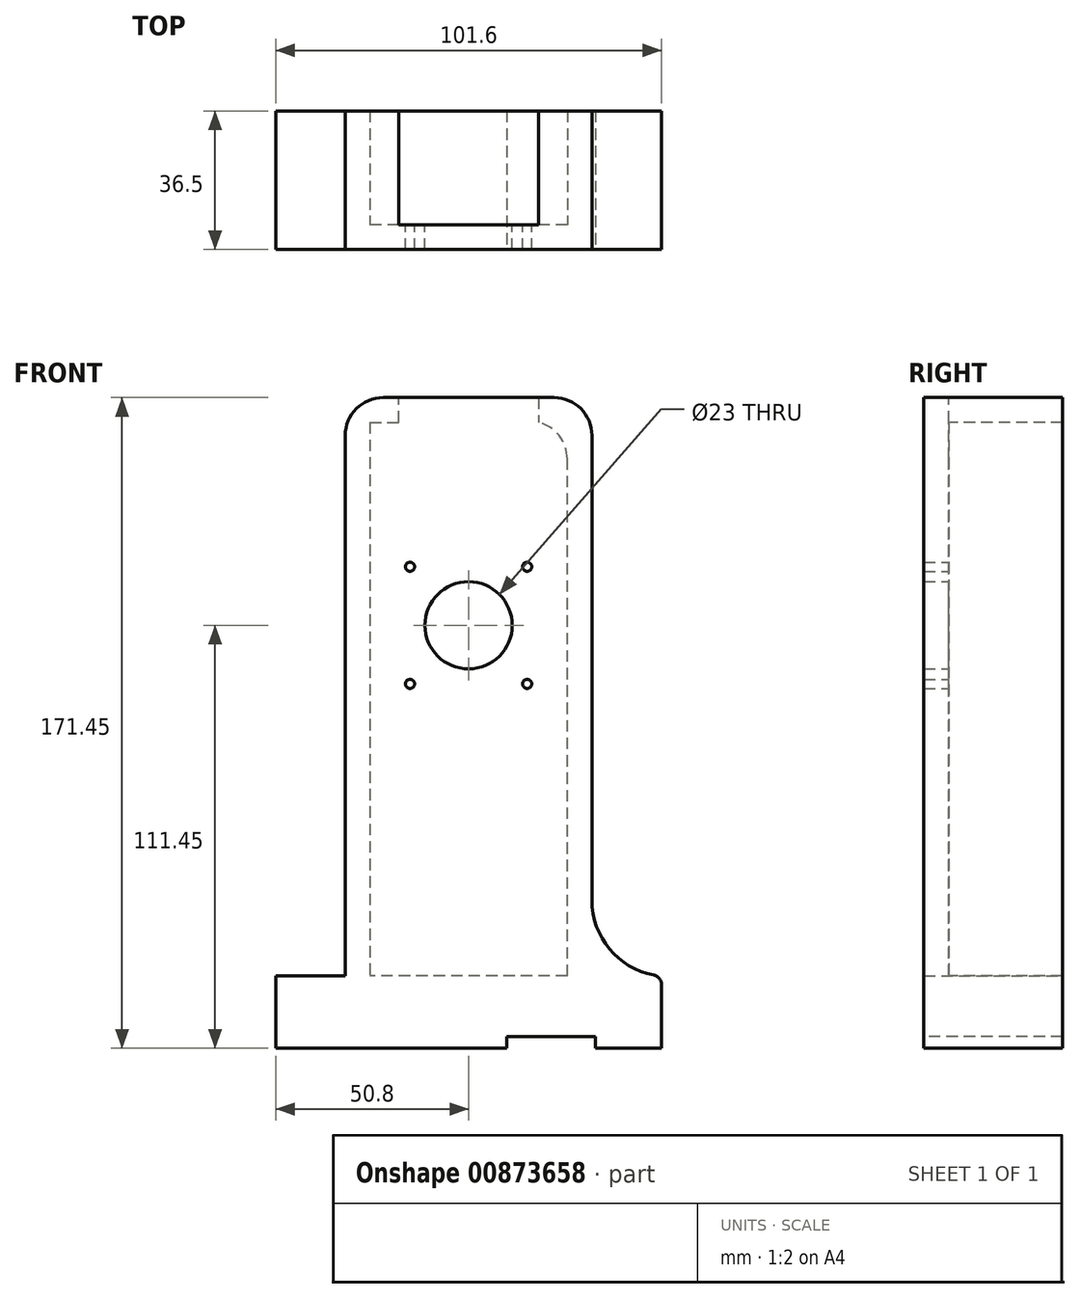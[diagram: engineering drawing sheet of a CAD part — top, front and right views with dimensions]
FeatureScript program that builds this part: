
annotation { "Feature Type Name" : "Feature", "Feature Type Description" : "" }
export const myFeature = defineFeature(function(context is Context, id is Id, definition is map)
    precondition{}
    {
        {
            var Q0;
            Q0=qCreatedBy(makeId("Front.planeOp"),FACE);
            var sketch = newSketch(context, id + "F0", { "sketchPlane" : qUnion([Q0])});
            skLineSegment(sketch, "E0.bottom", {"start": v(-32.5, 76.2) * mm, "end": v(32.5, 76.2) * mm});
            skLineSegment(sketch, "E0.top", {"start": v(-32.5, -76.2) * mm, "end": v(32.5, -76.2) * mm});
            skLineSegment(sketch, "E0.left", {"start": v(-32.5, 76.2) * mm, "end": v(-32.5, -76.2) * mm});
            skLineSegment(sketch, "E0.right", {"start": v(32.5, 76.2) * mm, "end": v(32.5, -76.2) * mm});
            skPoint(sketch, "E0.middle", {"position": v(0, 0) * mm});
            skLineSegment(sketch, "E1", {"start": v(0, 76.2) * mm, "end": v(0, -76.2) * mm, "construction": true});
            skLineSegment(sketch, "E2.bottom", {"start": v(-15.43, 31.63) * mm, "end": v(15.43, 31.63) * mm, "construction": true});
            skLineSegment(sketch, "E2.top", {"start": v(-15.43, 0.77) * mm, "end": v(15.43, 0.77) * mm, "construction": true});
            skLineSegment(sketch, "E2.left", {"start": v(-15.43, 31.63) * mm, "end": v(-15.43, 0.77) * mm, "construction": true});
            skLineSegment(sketch, "E2.right", {"start": v(15.43, 31.63) * mm, "end": v(15.43, 0.77) * mm, "construction": true});
            skPoint(sketch, "E2.middle", {"position": v(0, 16.2) * mm});
            skCircle(sketch, "E3", {"center": v(-15.43, 31.63) * mm, "radius": 1.2 * mm});
            skCircle(sketch, "E4", {"center": v(15.43, 31.63) * mm, "radius": 1.2 * mm});
            skCircle(sketch, "E5", {"center": v(15.43, 0.77) * mm, "radius": 1.2 * mm});
            skCircle(sketch, "E6", {"center": v(-15.43, 0.77) * mm, "radius": 1.2 * mm});
            skCircle(sketch, "E7", {"center": v(0, 16.2) * mm, "radius": 11.5 * mm});
            skSolve(sketch);
        }
        {
            var Q0;
            Q0=makeQuery(id+"F0.imprint","IMPRINT",FACE,{"disambiguationData":[TD([[makeQuery(id+"F0.imprint","IMPRINT",EDGE,{"derivedFrom":sQuery(id+"F0.wireOp",EDGE,"E0.bottom")}),-1.0]])]});
            extrude(context, id + "F1", {"entities" : qUnion([Q0]), "depth" : 6.5 * mm, "offsetDistance" : 25.4 * mm});
        }
        {
            var Q0;
            Q0=makeQuery(id+"F1.opExtrude","CAP_FACE",FACE,{"disambiguationData":[OSD([sQuery(id+"F0.wireOp",EDGE,"E0.bottom"),sQuery(id+"F0.wireOp",EDGE,"E0.top"),sQuery(id+"F0.wireOp",EDGE,"E0.left"),sQuery(id+"F0.wireOp",EDGE,"E0.right"),sQuery(id+"F0.wireOp",EDGE,"E3"),sQuery(id+"F0.wireOp",EDGE,"E4"),sQuery(id+"F0.wireOp",EDGE,"E5"),sQuery(id+"F0.wireOp",EDGE,"E6"),sQuery(id+"F0.wireOp",EDGE,"E7")])],"isStart":true});
            var sketch = newSketch(context, id + "F2", { "sketchPlane" : qUnion([Q0])});
            skLineSegment(sketch, "E8", {"start": v(-32.5, 76.2) * mm, "end": v(-32.5, -76.2) * mm});
            skLineSegment(sketch, "E9", {"start": v(-32.5, -76.2) * mm, "end": v(-26, -76.2) * mm});
            skLineSegment(sketch, "E10", {"start": v(-26, -76.2) * mm, "end": v(-26, 69.7) * mm});
            skLineSegment(sketch, "E11", {"start": v(26, 69.7) * mm, "end": v(26, -76.2) * mm});
            skLineSegment(sketch, "E12", {"start": v(26, -76.2) * mm, "end": v(32.5, -76.2) * mm});
            skLineSegment(sketch, "E13", {"start": v(32.5, -76.2) * mm, "end": v(32.5, 76.2) * mm});
            skLineSegment(sketch, "E14", {"start": v(-32.5, 76.2) * mm, "end": v(-18.41, 76.2) * mm});
            skLineSegment(sketch, "E15", {"start": v(26, 69.7) * mm, "end": v(18.38, 69.7) * mm});
            skLineSegment(sketch, "E16", {"start": v(18.38, 69.7) * mm, "end": v(18.38, 76.2) * mm});
            skLineSegment(sketch, "E17", {"start": v(18.38, 76.2) * mm, "end": v(32.5, 76.2) * mm});
            skLineSegment(sketch, "E18", {"start": v(-18.41, 76.2) * mm, "end": v(-18.41, 69.7) * mm});
            skLineSegment(sketch, "E19", {"start": v(-26, 69.7) * mm, "end": v(-18.41, 69.7) * mm});
            skSolve(sketch);
        }
        {
            var Q0;
            Q0=makeQuery(id+"F2.imprint","IMPRINT",FACE,{"disambiguationData":[TD([[makeQuery(id+"F2.imprint","IMPRINT",EDGE,{"derivedFrom":sQuery(id+"F2.wireOp",EDGE,"E8")}),1.0]])]});
            extrude(context, id + "F3", {"entities" : qUnion([Q0]), "operationType" : NewBodyOperationType.ADD, "depth" : 30 * mm, "offsetDistance" : 25.4 * mm});
        }
        {
            var Q0;
            Q0=makeQuery(id+"F3.boolean.opBoolean","MERGE",EDGE,{"derivedFrom":[makeQuery(id+"F1.opExtrude","SWEPT_EDGE",EDGE,{"disambiguationData":[OSD([sQuery(id+"F0.wireOp",EDGE,"E0.bottom"),sQuery(id+"F0.wireOp",EDGE,"E0.right")])]}),makeQuery(id+"F3.opExtrude","SWEPT_EDGE",EDGE,{"disambiguationData":[OSD([sQuery(id+"F2.wireOp",EDGE,"E8"),sQuery(id+"F2.wireOp",EDGE,"top9ZBjK-HaFo-sFNs-O2iO-FRZwXBmGVt9y")])]})]});
            var Q1;
            Q1=makeQuery(id+"F3.boolean.opBoolean","MERGE",EDGE,{"derivedFrom":[makeQuery(id+"F1.opExtrude","SWEPT_EDGE",EDGE,{"disambiguationData":[OSD([sQuery(id+"F0.wireOp",EDGE,"E0.bottom"),sQuery(id+"F0.wireOp",EDGE,"E0.left")])]}),makeQuery(id+"F3.opExtrude","SWEPT_EDGE",EDGE,{"disambiguationData":[OSD([sQuery(id+"F2.wireOp",EDGE,"E13"),sQuery(id+"F2.wireOp",EDGE,"top9ZBjK-HaFo-sFNs-O2iO-FRZwXBmGVt9y")])]})]});
            var Q2;
            Q2=makeQuery(id+"F3.opExtrude","SWEPT_EDGE",EDGE,{"disambiguationData":[OSD([sQuery(id+"F2.wireOp",EDGE,"E10"),sQuery(id+"F2.wireOp",EDGE,"qCY2hAou-IPp3-AkAy-DybL-IcWh8WlS5N6P")])]});
            var Q3;
            Q3=makeQuery(id+"F3.opExtrude","SWEPT_EDGE",EDGE,{"disambiguationData":[OSD([sQuery(id+"F2.wireOp",EDGE,"qCY2hAou-IPp3-AkAy-DybL-IcWh8WlS5N6P"),sQuery(id+"F2.wireOp",EDGE,"E11")])]});
            fillet(context, id + "F4", {"entities" : qUnion([Q0, Q1, Q2, Q3]), "radius" : 10 * mm, "tangentPropagation" : true, "allowEdgeOverflow" : false});
        }
        {
            var Q0;
            Q0=qCreatedBy(makeId("Front.planeOp"),FACE);
            var sketch = newSketch(context, id + "F5", { "sketchPlane" : qUnion([Q0])});
            skLineSegment(sketch, "E20", {"start": v(0, 0) * mm, "end": v(0, -76.2) * mm, "construction": true});
            skLineSegment(sketch, "E21", {"start": v(0, -76.2) * mm, "end": v(0, -95.25) * mm, "construction": true});
            skLineSegment(sketch, "E22.bottom", {"start": v(-50.8, -95.25) * mm, "end": v(50.8, -95.25) * mm});
            skLineSegment(sketch, "E22.top", {"start": v(-50.8, -76.2) * mm, "end": v(50.8, -76.2) * mm});
            skLineSegment(sketch, "E22.left", {"start": v(-50.8, -95.25) * mm, "end": v(-50.8, -76.2) * mm});
            skLineSegment(sketch, "E22.right", {"start": v(50.8, -95.25) * mm, "end": v(50.8, -76.2) * mm});
            skPoint(sketch, "E22.middle", {"position": v(0, -85.72) * mm});
            skSolve(sketch);
        }
        {
            var Q0;
            Q0=makeQuery(id+"F5.imprint","IMPRINT",FACE,{"disambiguationData":[TD([[makeQuery(id+"F5.imprint","IMPRINT",EDGE,{"derivedFrom":sQuery(id+"F5.wireOp",EDGE,"E22.bottom")}),1.0]])]});
            extrude(context, id + "F6", {"entities" : qUnion([Q0]), "operationType" : NewBodyOperationType.ADD, "depth" : 6.5 * mm, "offsetDistance" : 25.4 * mm});
        }
        {
            var Q0;
            Q0=makeQuery(id+"F6.boolean.opBoolean","MERGE",FACE,{"derivedFrom":[makeQuery(id+"F1.opExtrude","CAP_FACE",FACE,{"disambiguationData":[OSD([sQuery(id+"F0.wireOp",EDGE,"E0.bottom"),sQuery(id+"F0.wireOp",EDGE,"E0.top"),sQuery(id+"F0.wireOp",EDGE,"E0.left"),sQuery(id+"F0.wireOp",EDGE,"E0.right"),sQuery(id+"F0.wireOp",EDGE,"E3"),sQuery(id+"F0.wireOp",EDGE,"E4"),sQuery(id+"F0.wireOp",EDGE,"E5"),sQuery(id+"F0.wireOp",EDGE,"E6"),sQuery(id+"F0.wireOp",EDGE,"E7")])],"isStart":true}),makeQuery(id+"F6.opExtrude","CAP_FACE",FACE,{"disambiguationData":[OSD([sQuery(id+"F5.wireOp",EDGE,"E22.bottom"),sQuery(id+"F5.wireOp",EDGE,"E22.top"),sQuery(id+"F5.wireOp",EDGE,"E22.left"),sQuery(id+"F5.wireOp",EDGE,"E22.right")])],"isStart":true})]});
            var sketch = newSketch(context, id + "F7", { "sketchPlane" : qUnion([Q0])});
            skLineSegment(sketch, "E23.bottom", {"start": v(-50.8, -76.2) * mm, "end": v(50.8, -76.2) * mm});
            skLineSegment(sketch, "E23.top", {"start": v(-50.8, -95.25) * mm, "end": v(50.8, -95.25) * mm});
            skLineSegment(sketch, "E23.left", {"start": v(-50.8, -76.2) * mm, "end": v(-50.8, -95.25) * mm});
            skLineSegment(sketch, "E23.right", {"start": v(50.8, -76.2) * mm, "end": v(50.8, -95.25) * mm});
            skPoint(sketch, "E23.middle", {"position": v(0, -85.72) * mm});
            skPoint(sketch, "E23.middle.positionSnap0", {"position": v(-50.8, -85.72) * mm});
            skPoint(sketch, "E23.centerSnap0", {"position": v(-50.8, -85.72) * mm});
            skSolve(sketch);
        }
        {
            var Q0;
            Q0 = qSketchRegion(id + "F7", true);
            extrude(context, id + "F8", {"entities" : qUnion([Q0]), "operationType" : NewBodyOperationType.ADD, "depth" : 30 * mm, "offsetDistance" : 25.4 * mm});
        }
        {
            var Q0;
            {var subQ0=sQuery(id+"F0.wireOp",EDGE,"E0.left");var subQ2=sQuery(id+"F2.wireOp",EDGE,"E13");var subQ4=sQuery(id+"F2.wireOp",EDGE,"E12");var subQ5=sQuery(id+"F0.wireOp",EDGE,"E0.top");var subQ6=makeQuery(id+"F3.boolean.opBoolean","MERGE",EDGE,{"derivedFrom":[makeQuery(id+"F1.opExtrude","SWEPT_EDGE",EDGE,{"disambiguationData":[OSD([subQ5,subQ0])]}),makeQuery(id+"F3.opExtrude","SWEPT_EDGE",EDGE,{"disambiguationData":[OSD([subQ4,subQ2])]})]});Q0=makeQuery(id+"F8.boolean.opBoolean","MERGE",EDGE,{"derivedFrom":[makeQuery(id+"F6.boolean.opBoolean","SPLIT",EDGE,{"disambiguationData":[topologyDisambiguationEdgeConnected([makeQuery(id+"F1.opExtrude","SWEPT_FACE",FACE,{"disambiguationData":[OSD([subQ5])]})])],"derivedFrom":subQ6}),makeQuery(id+"F6.boolean.opBoolean","SPLIT",EDGE,{"disambiguationData":[topologyDisambiguationEdgeConnected([makeQuery(id+"F6.opExtrude","SWEPT_FACE",FACE,{"disambiguationData":[OSD([sQuery(id+"F5.wireOp",EDGE,"E22.top")])]})])],"derivedFrom":subQ6})]});}
            var Q1;
            {var subQ0=sQuery(id+"F0.wireOp",EDGE,"E0.right");var subQ2=sQuery(id+"F2.wireOp",EDGE,"E8");var subQ4=sQuery(id+"F2.wireOp",EDGE,"E9");var subQ5=sQuery(id+"F0.wireOp",EDGE,"E0.top");var subQ6=makeQuery(id+"F3.boolean.opBoolean","MERGE",EDGE,{"derivedFrom":[makeQuery(id+"F1.opExtrude","SWEPT_EDGE",EDGE,{"disambiguationData":[OSD([subQ5,subQ0])]}),makeQuery(id+"F3.opExtrude","SWEPT_EDGE",EDGE,{"disambiguationData":[OSD([subQ2,subQ4])]})]});Q1=makeQuery(id+"F8.boolean.opBoolean","MERGE",EDGE,{"derivedFrom":[makeQuery(id+"F6.boolean.opBoolean","SPLIT",EDGE,{"disambiguationData":[topologyDisambiguationEdgeConnected([makeQuery(id+"F1.opExtrude","SWEPT_FACE",FACE,{"disambiguationData":[OSD([subQ5])]})])],"derivedFrom":subQ6}),makeQuery(id+"F6.boolean.opBoolean","SPLIT",EDGE,{"disambiguationData":[topologyDisambiguationEdgeConnected([makeQuery(id+"F6.opExtrude","SWEPT_FACE",FACE,{"disambiguationData":[OSD([sQuery(id+"F5.wireOp",EDGE,"E22.top")])]})])],"derivedFrom":subQ6})]});}
            fillet(context, id + "F9", {"entities" : qUnion([Q0, Q1]), "radius" : 20 * mm, "tangentPropagation" : true, "allowEdgeOverflow" : false});
        }
        {
            var Q0;
            {var subQ0=sQuery(id+"F0.wireOp",EDGE,"E0.left");var subQ2=sQuery(id+"F2.wireOp",EDGE,"E13");var subQ4=sQuery(id+"F2.wireOp",EDGE,"E12");var subQ5=sQuery(id+"F0.wireOp",EDGE,"E0.top");var subQ6=makeQuery(id+"F3.boolean.opBoolean","MERGE",EDGE,{"derivedFrom":[makeQuery(id+"F1.opExtrude","SWEPT_EDGE",EDGE,{"disambiguationData":[OSD([subQ5,subQ0])]}),makeQuery(id+"F3.opExtrude","SWEPT_EDGE",EDGE,{"disambiguationData":[OSD([subQ4,subQ2])]})]});Q0=makeQuery(id+"F9.opFillet","BLEND_EDGE",EDGE,{"blendedFrom":[makeQuery(id+"F8.boolean.opBoolean","MERGE",EDGE,{"derivedFrom":[makeQuery(id+"F6.boolean.opBoolean","SPLIT",EDGE,{"disambiguationData":[topologyDisambiguationEdgeConnected([makeQuery(id+"F1.opExtrude","SWEPT_FACE",FACE,{"disambiguationData":[OSD([subQ5])]})])],"derivedFrom":subQ6}),makeQuery(id+"F6.boolean.opBoolean","SPLIT",EDGE,{"disambiguationData":[topologyDisambiguationEdgeConnected([makeQuery(id+"F6.opExtrude","SWEPT_FACE",FACE,{"disambiguationData":[OSD([sQuery(id+"F5.wireOp",EDGE,"E22.top")])]})])],"derivedFrom":subQ6})]}),makeQuery(id+"F8.boolean.opBoolean","MERGE",FACE,{"derivedFrom":[makeQuery(id+"F6.opExtrude","SWEPT_FACE",FACE,{"disambiguationData":[OSD([sQuery(id+"F5.wireOp",EDGE,"E22.left")])]}),makeQuery(id+"F8.opExtrude","SWEPT_FACE",FACE,{"disambiguationData":[OSD([sQuery(id+"F7.wireOp",EDGE,"E23.right")])]})]})],"blendedInto":[makeQuery(id+"F8.boolean.opBoolean","MERGE",FACE,{"derivedFrom":[makeQuery(id+"F6.opExtrude","SWEPT_FACE",FACE,{"disambiguationData":[OSD([sQuery(id+"F5.wireOp",EDGE,"E22.left")])]}),makeQuery(id+"F8.opExtrude","SWEPT_FACE",FACE,{"disambiguationData":[OSD([sQuery(id+"F7.wireOp",EDGE,"E23.right")])]})]})]});}
            var Q1;
            {var subQ0=sQuery(id+"F0.wireOp",EDGE,"E0.right");var subQ2=sQuery(id+"F2.wireOp",EDGE,"E8");var subQ4=sQuery(id+"F2.wireOp",EDGE,"E9");var subQ5=sQuery(id+"F0.wireOp",EDGE,"E0.top");var subQ6=makeQuery(id+"F3.boolean.opBoolean","MERGE",EDGE,{"derivedFrom":[makeQuery(id+"F1.opExtrude","SWEPT_EDGE",EDGE,{"disambiguationData":[OSD([subQ5,subQ0])]}),makeQuery(id+"F3.opExtrude","SWEPT_EDGE",EDGE,{"disambiguationData":[OSD([subQ2,subQ4])]})]});Q1=makeQuery(id+"F9.opFillet","BLEND_EDGE",EDGE,{"blendedFrom":[makeQuery(id+"F8.boolean.opBoolean","MERGE",EDGE,{"derivedFrom":[makeQuery(id+"F6.boolean.opBoolean","SPLIT",EDGE,{"disambiguationData":[topologyDisambiguationEdgeConnected([makeQuery(id+"F1.opExtrude","SWEPT_FACE",FACE,{"disambiguationData":[OSD([subQ5])]})])],"derivedFrom":subQ6}),makeQuery(id+"F6.boolean.opBoolean","SPLIT",EDGE,{"disambiguationData":[topologyDisambiguationEdgeConnected([makeQuery(id+"F6.opExtrude","SWEPT_FACE",FACE,{"disambiguationData":[OSD([sQuery(id+"F5.wireOp",EDGE,"E22.top")])]})])],"derivedFrom":subQ6})]}),makeQuery(id+"F8.boolean.opBoolean","MERGE",FACE,{"derivedFrom":[makeQuery(id+"F6.opExtrude","SWEPT_FACE",FACE,{"disambiguationData":[OSD([sQuery(id+"F5.wireOp",EDGE,"E22.right")])]}),makeQuery(id+"F8.opExtrude","SWEPT_FACE",FACE,{"disambiguationData":[OSD([sQuery(id+"F7.wireOp",EDGE,"E23.left")])]})]})],"blendedInto":[makeQuery(id+"F8.boolean.opBoolean","MERGE",FACE,{"derivedFrom":[makeQuery(id+"F6.opExtrude","SWEPT_FACE",FACE,{"disambiguationData":[OSD([sQuery(id+"F5.wireOp",EDGE,"E22.right")])]}),makeQuery(id+"F8.opExtrude","SWEPT_FACE",FACE,{"disambiguationData":[OSD([sQuery(id+"F7.wireOp",EDGE,"E23.left")])]})]})]});}
            fillet(context, id + "F10", {"entities" : qUnion([Q0, Q1]), "radius" : 2.5 * mm, "tangentPropagation" : true, "allowEdgeOverflow" : false});
        }
        {
            var Q0;
            Q0=makeQuery(id+"F6.boolean.opBoolean","MERGE",FACE,{"derivedFrom":[makeQuery(id+"F1.opExtrude","CAP_FACE",FACE,{"disambiguationData":[OSD([sQuery(id+"F0.wireOp",EDGE,"E0.bottom"),sQuery(id+"F0.wireOp",EDGE,"E0.top"),sQuery(id+"F0.wireOp",EDGE,"E0.left"),sQuery(id+"F0.wireOp",EDGE,"E0.right"),sQuery(id+"F0.wireOp",EDGE,"E3"),sQuery(id+"F0.wireOp",EDGE,"E4"),sQuery(id+"F0.wireOp",EDGE,"E5"),sQuery(id+"F0.wireOp",EDGE,"E6"),sQuery(id+"F0.wireOp",EDGE,"E7")])],"isStart":false}),makeQuery(id+"F6.opExtrude","CAP_FACE",FACE,{"disambiguationData":[OSD([sQuery(id+"F5.wireOp",EDGE,"E22.bottom"),sQuery(id+"F5.wireOp",EDGE,"E22.top"),sQuery(id+"F5.wireOp",EDGE,"E22.left"),sQuery(id+"F5.wireOp",EDGE,"E22.right")])],"isStart":false})]});
            var sketch = newSketch(context, id + "F11", { "sketchPlane" : qUnion([Q0])});
            skLineSegment(sketch, "E24.bottom", {"start": v(10.1, -95.25) * mm, "end": v(33.42, -95.25) * mm});
            skLineSegment(sketch, "E24.top", {"start": v(10.1, -92.1) * mm, "end": v(33.42, -92.1) * mm});
            skLineSegment(sketch, "E24.left", {"start": v(10.1, -95.25) * mm, "end": v(10.1, -92.1) * mm});
            skLineSegment(sketch, "E24.right", {"start": v(33.42, -95.25) * mm, "end": v(33.42, -92.1) * mm});
            skSolve(sketch);
        }
        {
            var Q0;
            Q0 = qSketchRegion(id + "F11", true);
            extrude(context, id + "F12", {"entities" : qUnion([Q0]), "operationType" : NewBodyOperationType.REMOVE, "oppositeDirection" : true, "depth" : 36.5 * mm, "offsetDistance" : 25.4 * mm});
        }
        {
            var Q0;
            Q0=makeQuery(id+"F2.imprint","IMPRINT",FACE,{"disambiguationData":[TD([[makeQuery(id+"F2.imprint","IMPRINT",EDGE,{"derivedFrom":sQuery(id+"F2.wireOp",EDGE,"E11")}),1.0]])]});
            extrude(context, id + "F13", {"entities" : qUnion([Q0]), "operationType" : NewBodyOperationType.ADD, "depth" : 30 * mm, "offsetDistance" : 25.4 * mm});
        }
        {
            var Q0;
            Q0=makeQuery(id+"F13.boolean.opBoolean","MERGE",EDGE,{"derivedFrom":[makeQuery(id+"F1.opExtrude","SWEPT_EDGE",EDGE,{"disambiguationData":[OSD([sQuery(id+"F0.wireOp",EDGE,"E0.bottom"),sQuery(id+"F0.wireOp",EDGE,"E0.left")])]}),makeQuery(id+"F13.opExtrude","SWEPT_EDGE",EDGE,{"disambiguationData":[OSD([sQuery(id+"F2.wireOp",EDGE,"E13"),sQuery(id+"F2.wireOp",EDGE,"E17")])]})]});
            fillet(context, id + "F14", {"entities" : qUnion([Q0]), "radius" : 10 * mm, "tangentPropagation" : true, "allowEdgeOverflow" : false});
        }
    });
